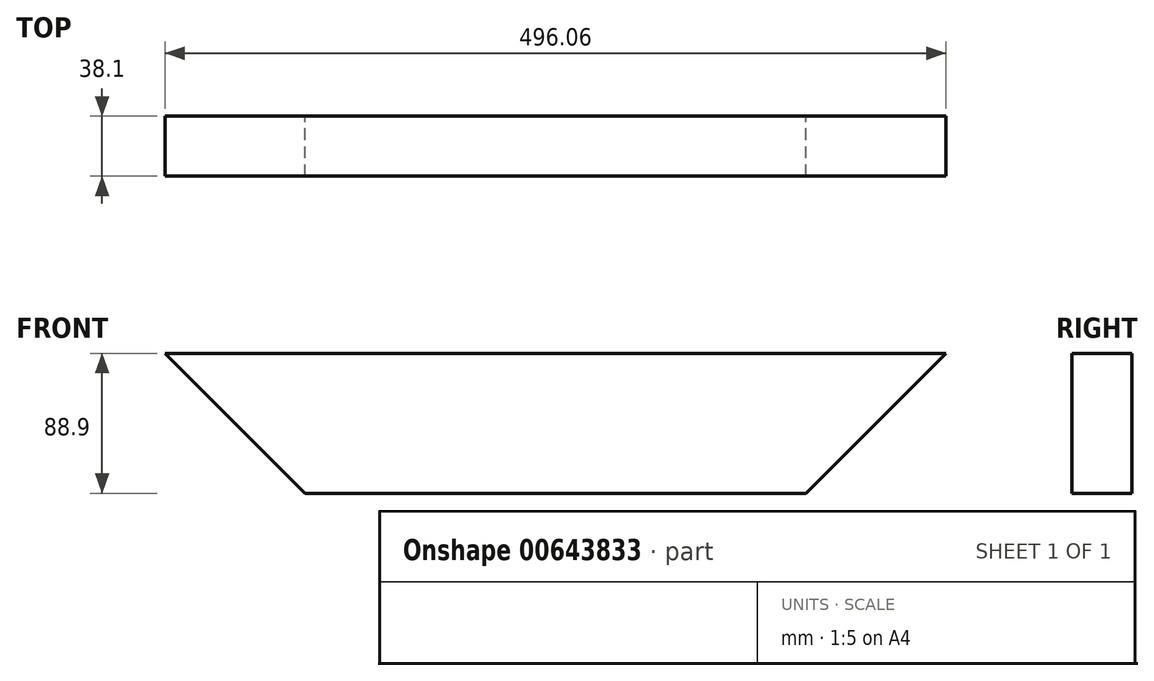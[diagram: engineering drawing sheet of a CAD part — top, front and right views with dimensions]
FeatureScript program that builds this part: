
annotation { "Feature Type Name" : "Feature", "Feature Type Description" : "" }
export const myFeature = defineFeature(function(context is Context, id is Id, definition is map)
    precondition{}
    {
        {
            var Q0;
            Q0=qCreatedBy(makeId("Front.planeOp"),FACE);
            var sketch = newSketch(context, id + "F0", { "sketchPlane" : qUnion([Q0])});
            skLineSegment(sketch, "E0.bottom", {"start": v(248.72, 0) * mm, "end": v(-247.34, 0) * mm});
            skLineSegment(sketch, "E0.top", {"start": v(248.72, 88.9) * mm, "end": v(-247.34, 88.9) * mm});
            skLineSegment(sketch, "E0.left", {"start": v(248.72, 0) * mm, "end": v(248.72, 88.9) * mm});
            skLineSegment(sketch, "E0.right", {"start": v(-247.34, 0) * mm, "end": v(-247.34, 88.9) * mm});
            skPoint(sketch, "E0.middle", {"position": v(0.69, 44.45) * mm});
            skLineSegment(sketch, "E1", {"start": v(248.72, 88.9) * mm, "end": v(159.82, 0) * mm});
            skLineSegment(sketch, "E2", {"start": v(-247.34, 88.9) * mm, "end": v(-158.44, 0) * mm});
            skSolve(sketch);
        }
        {
            var Q0;
            Q0 = qSketchRegion(id + "F0", true);
            extrude(context, id + "F1", {"entities" : qUnion([Q0]), "depth" : 38.1 * mm, "offsetDistance" : 25.4 * mm});
        }
        {
            var Q0;
            {var subQ0=sQuery(id+"F0.wireOp",EDGE,"E0.right");Q0=makeQuery(id+"F0.imprint","IMPRINT",FACE,{"disambiguationData":[TD([[makeQuery(id+"F0.imprint","IMPRINT",EDGE,{"derivedFrom":subQ0}),-1.0]])]});}
            extrude(context, id + "F2", {"entities" : qUnion([Q0]), "operationType" : NewBodyOperationType.REMOVE, "oppositeDirection" : true, "depth" : -38.1 * mm, "offsetDistance" : 25.4 * mm});
        }
        {
            var Q0;
            {var subQ0=sQuery(id+"F0.wireOp",EDGE,"E0.left");Q0=makeQuery(id+"F0.imprint","IMPRINT",FACE,{"disambiguationData":[TD([[makeQuery(id+"F0.imprint","IMPRINT",EDGE,{"derivedFrom":subQ0}),1.0]])]});}
            extrude(context, id + "F3", {"entities" : qUnion([Q0]), "operationType" : NewBodyOperationType.REMOVE, "oppositeDirection" : true, "depth" : -38.1 * mm, "offsetDistance" : 25.4 * mm});
        }
    });
